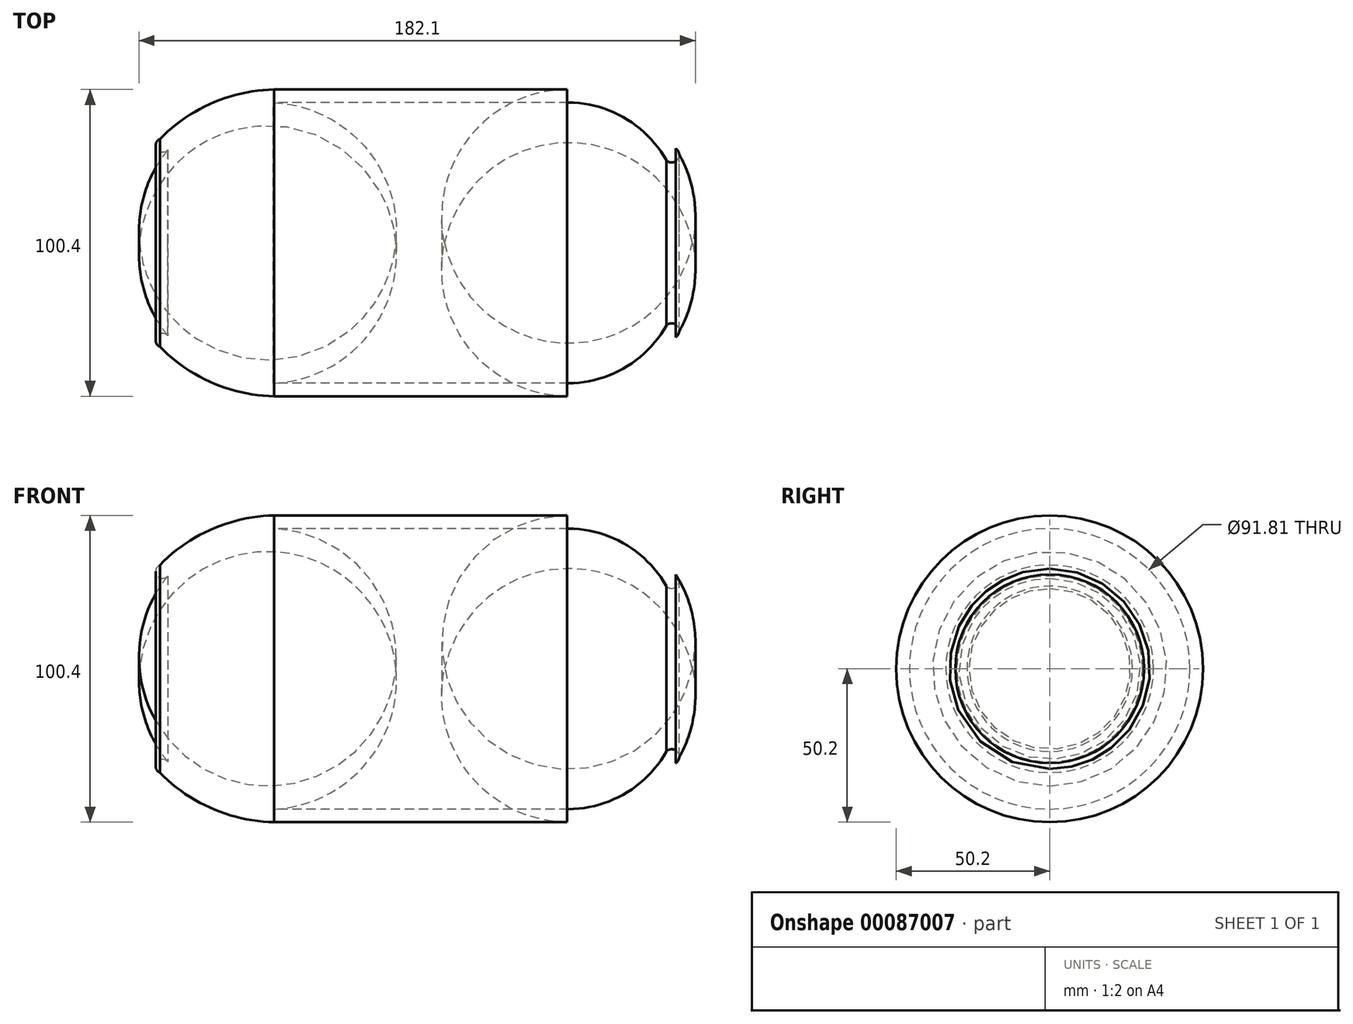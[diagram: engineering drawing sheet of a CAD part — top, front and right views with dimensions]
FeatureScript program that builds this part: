
annotation { "Feature Type Name" : "Feature", "Feature Type Description" : "" }
export const myFeature = defineFeature(function(context is Context, id is Id, definition is map)
    precondition{}
    {
        {
            var Q0;
            Q0=qCreatedBy(makeId("Top.planeOp"),FACE);
            var sketch = newSketch(context, id + "F0", { "sketchPlane" : qUnion([Q0])});
            skArc(sketch, "E0", {"start": v(-54.73, 50.2) * mm, "mid": v(-75.04, 45.76) * mm, "end": v(-92.17, 33.98) * mm});
            skArc(sketch, "E1", {"start": v(-54.97, 45.9) * mm, "mid": v(-74.1, 42.26) * mm, "end": v(-89.55, 30.4) * mm});
            skArc(sketch, "E2", {"start": v(76.67, 30.88) * mm, "mid": v(61.42, 45.16) * mm, "end": v(41.14, 50.2) * mm});
            skArc(sketch, "E3", {"start": v(73.57, 27.07) * mm, "mid": v(60.13, 40.78) * mm, "end": v(41.61, 45.9) * mm});
            skLineSegment(sketch, "E4", {"start": v(41.14, 50.2) * mm, "end": v(-54.73, 50.2) * mm});
            skLineSegment(sketch, "E5", {"start": v(-54.97, 45.9) * mm, "end": v(41.61, 45.9) * mm});
            skArc(sketch, "E6", {"start": v(-92.17, 33.98) * mm, "mid": v(-93.1, 30.55) * mm, "end": v(-89.55, 30.4) * mm});
            skArc(sketch, "E7", {"start": v(73.57, 27.07) * mm, "mid": v(77.26, 27.24) * mm, "end": v(76.67, 30.88) * mm});
            skLineSegment(sketch, "E8", {"start": v(-91.7, 0) * mm, "end": v(85.73, 0) * mm});
            skSolve(sketch);
        }
        {
            var Q0;
            Q0 = qSketchRegion(id + "F0", true);
            var Q1;
            Q1=sQuery(id+"F0.wireOp",EDGE,"E8");
            revolve(context, id + "F1", {"entities" : qUnion([Q0]), "axis" : qUnion([Q1]), "revolveType" : RevolveType.FULL});
        }
    });
